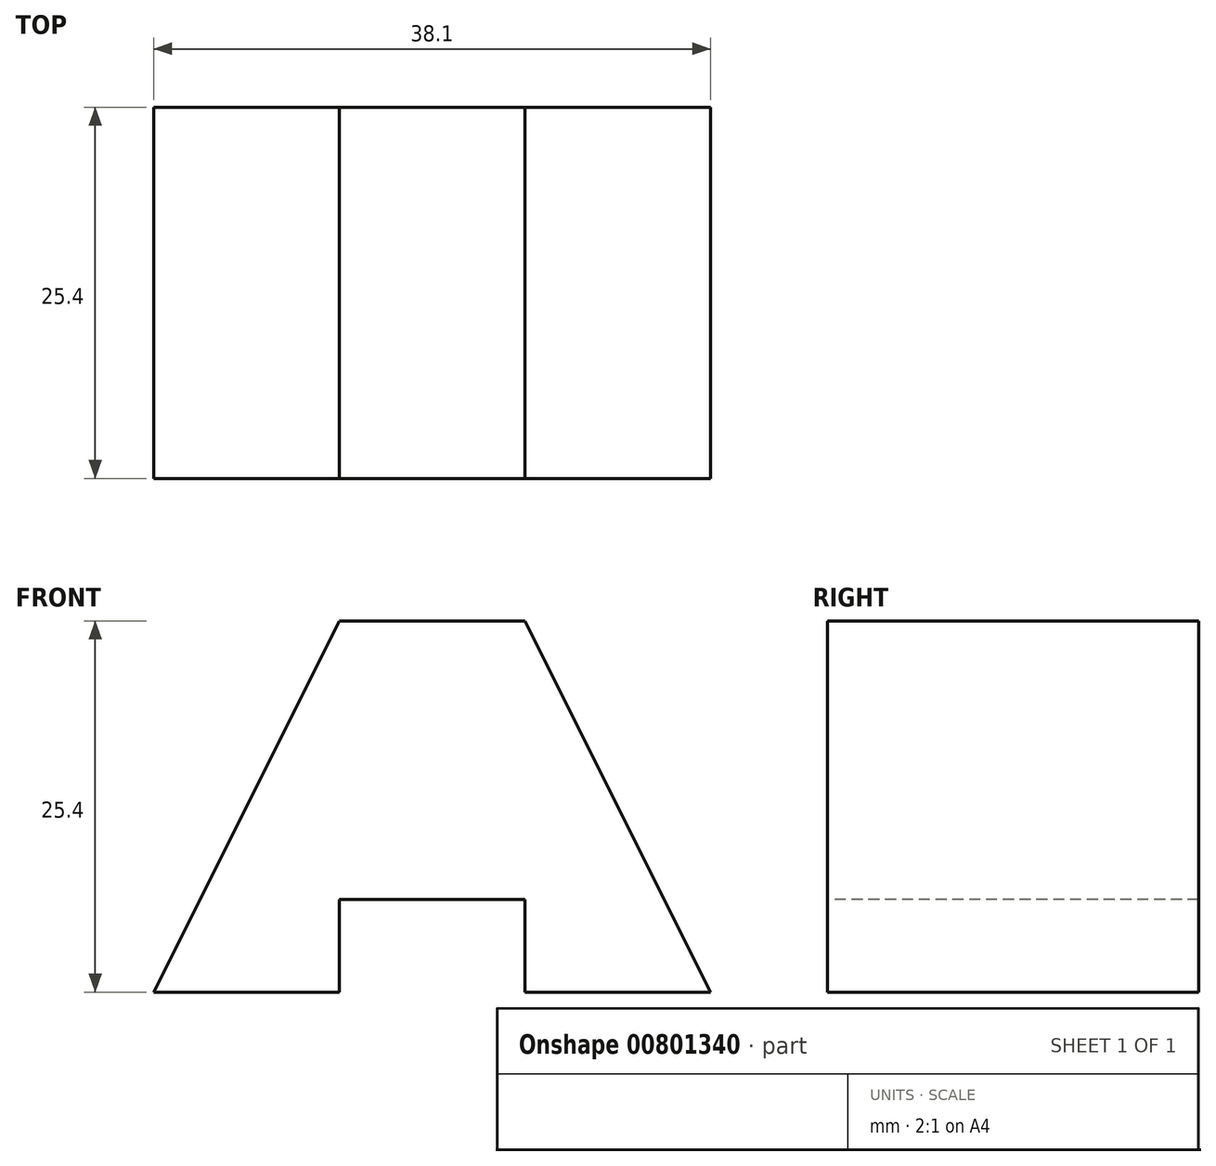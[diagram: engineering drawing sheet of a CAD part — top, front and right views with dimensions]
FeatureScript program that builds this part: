
annotation { "Feature Type Name" : "Feature", "Feature Type Description" : "" }
export const myFeature = defineFeature(function(context is Context, id is Id, definition is map)
    precondition{}
    {
        {
            var Q0;
            Q0=qCreatedBy(makeId("Front.planeOp"),FACE);
            var sketch = newSketch(context, id + "F0", { "sketchPlane" : qUnion([Q0])});
            skLineSegment(sketch, "E0", {"start": v(0, 0) * mm, "end": v(12.7, 0) * mm});
            skLineSegment(sketch, "E1", {"start": v(12.7, 0) * mm, "end": v(12.7, 6.35) * mm});
            skLineSegment(sketch, "E2", {"start": v(12.7, 6.35) * mm, "end": v(25.4, 6.35) * mm});
            skLineSegment(sketch, "E3", {"start": v(25.4, 6.35) * mm, "end": v(25.4, 0) * mm});
            skLineSegment(sketch, "E4", {"start": v(25.4, 0) * mm, "end": v(38.1, 0) * mm});
            skLineSegment(sketch, "E5", {"start": v(38.1, 0) * mm, "end": v(38.1, 25.4) * mm});
            skLineSegment(sketch, "E6", {"start": v(0, 0) * mm, "end": v(0, 25.4) * mm});
            skLineSegment(sketch, "E7", {"start": v(0, 25.4) * mm, "end": v(38.1, 25.4) * mm});
            skSolve(sketch);
        }
        {
            var Q0;
            Q0=qSketchRegion(id+"F0",true);
            extrude(context, id + "F1", {"entities" : qUnion([Q0]), "oppositeDirection" : true, "depth" : 25.4 * mm, "offsetDistance" : 25.4 * mm});
        }
        {
            var Q0;
            Q0=makeQuery(id+"F1.opExtrude","CAP_FACE",FACE,{"disambiguationData":[OSD([sQuery(id+"F0.wireOp",EDGE,"E0"),sQuery(id+"F0.wireOp",EDGE,"E1"),sQuery(id+"F0.wireOp",EDGE,"E2"),sQuery(id+"F0.wireOp",EDGE,"E3"),sQuery(id+"F0.wireOp",EDGE,"E4"),sQuery(id+"F0.wireOp",EDGE,"E5"),sQuery(id+"F0.wireOp",EDGE,"E6"),sQuery(id+"F0.wireOp",EDGE,"E7")])],"isStart":true});
            var sketch = newSketch(context, id + "F2", { "sketchPlane" : qUnion([Q0])});
            skLineSegment(sketch, "E8", {"start": v(0, 0) * mm, "end": v(12.7, 25.4) * mm});
            skLineSegment(sketch, "E9", {"start": v(38.1, 0) * mm, "end": v(25.4, 25.4) * mm});
            skLineSegment(sketch, "E10", {"start": v(25.4, 25.4) * mm, "end": v(38.1, 25.4) * mm});
            skLineSegment(sketch, "E11", {"start": v(38.1, 25.4) * mm, "end": v(38.1, 0) * mm});
            skLineSegment(sketch, "E12", {"start": v(12.7, 25.4) * mm, "end": v(0, 25.4) * mm});
            skLineSegment(sketch, "E13", {"start": v(0, 25.4) * mm, "end": v(0, 0) * mm});
            skSolve(sketch);
        }
        {
            var Q0;
            Q0=makeQuery(id+"F2.imprint","IMPRINT",FACE,{"disambiguationData":[TD([[makeQuery(id+"F2.imprint","IMPRINT",EDGE,{"derivedFrom":sQuery(id+"F2.wireOp",EDGE,"E8")}),1.0]])]});
            var Q1;
            Q1=makeQuery(id+"F2.imprint","IMPRINT",FACE,{"disambiguationData":[TD([[makeQuery(id+"F2.imprint","IMPRINT",EDGE,{"derivedFrom":sQuery(id+"F2.wireOp",EDGE,"E9")}),-1.0]])]});
            extrude(context, id + "F3", {"entities" : qUnion([Q0, Q1]), "operationType" : NewBodyOperationType.REMOVE, "oppositeDirection" : true, "depth" : 25.4 * mm, "offsetDistance" : 25.4 * mm});
        }
    });
